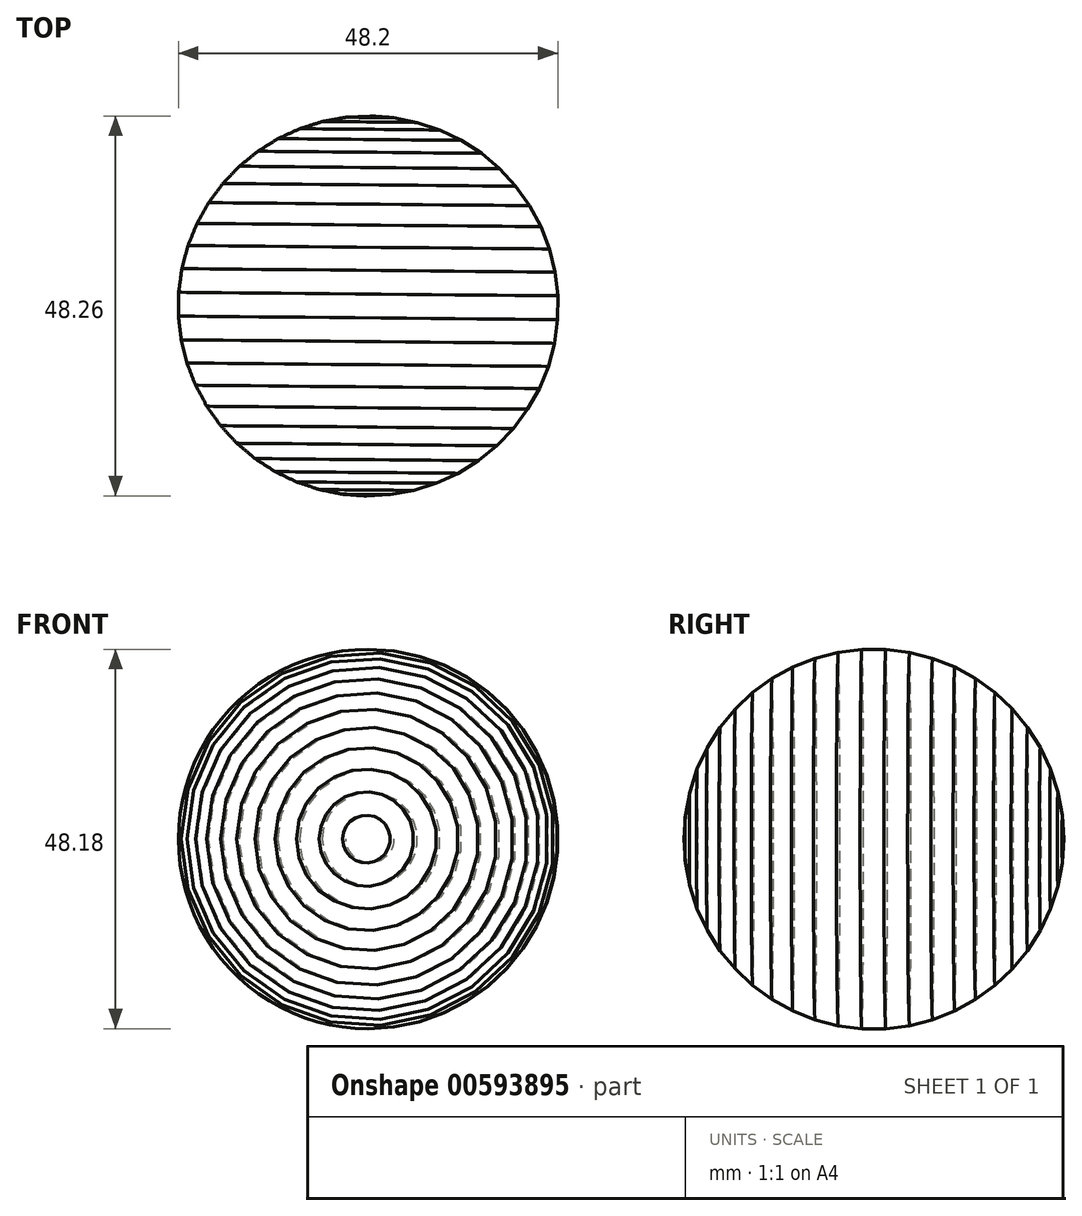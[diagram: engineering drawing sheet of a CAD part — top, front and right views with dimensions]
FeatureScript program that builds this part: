
annotation { "Feature Type Name" : "Feature", "Feature Type Description" : "" }
export const myFeature = defineFeature(function(context is Context, id is Id, definition is map)
    precondition{}
    {
        {
            var Q0;
            Q0=qCreatedBy(makeId("Top.planeOp"),FACE);
            var sketch = newSketch(context, id + "F0", { "sketchPlane" : qUnion([Q0])});
            skCircle(sketch, "E0.cCircle", {"center": v(0, 0) * mm, "radius": 24.09 * mm, "construction": true});
            skLineSegment(sketch, "E0.0", {"start": v(-21.74, 10.48) * mm, "end": v(-20.26, 13.12) * mm});
            skLineSegment(sketch, "E0.1", {"start": v(-20.26, 13.12) * mm, "end": v(-18.45, 15.56) * mm});
            skLineSegment(sketch, "E0.2", {"start": v(-18.45, 15.56) * mm, "end": v(-16.36, 17.75) * mm});
            skLineSegment(sketch, "E0.3", {"start": v(-16.36, 17.75) * mm, "end": v(-14, 19.66) * mm});
            skLineSegment(sketch, "E0.4", {"start": v(-14, 19.66) * mm, "end": v(-11.43, 21.26) * mm});
            skLineSegment(sketch, "E0.5", {"start": v(-11.43, 21.26) * mm, "end": v(-8.67, 22.52) * mm});
            skLineSegment(sketch, "E0.6", {"start": v(-8.67, 22.52) * mm, "end": v(-5.78, 23.43) * mm});
            skLineSegment(sketch, "E0.7", {"start": v(-5.78, 23.43) * mm, "end": v(-2.8, 23.97) * mm});
            skLineSegment(sketch, "E0.8", {"start": v(-2.8, 23.97) * mm, "end": v(0.23, 24.13) * mm});
            skLineSegment(sketch, "E0.9", {"start": v(0.23, 24.13) * mm, "end": v(3.25, 23.92) * mm});
            skLineSegment(sketch, "E0.10", {"start": v(3.25, 23.92) * mm, "end": v(6.22, 23.32) * mm});
            skLineSegment(sketch, "E0.11", {"start": v(6.22, 23.32) * mm, "end": v(9.1, 22.36) * mm});
            skLineSegment(sketch, "E0.12", {"start": v(9.1, 22.36) * mm, "end": v(11.83, 21.04) * mm});
            skLineSegment(sketch, "E0.13", {"start": v(11.83, 21.04) * mm, "end": v(14.37, 19.4) * mm});
            skLineSegment(sketch, "E0.14", {"start": v(14.37, 19.4) * mm, "end": v(16.69, 17.44) * mm});
            skLineSegment(sketch, "E0.15", {"start": v(16.69, 17.44) * mm, "end": v(18.74, 15.2) * mm});
            skLineSegment(sketch, "E0.16", {"start": v(18.74, 15.2) * mm, "end": v(20.5, 12.74) * mm});
            skLineSegment(sketch, "E0.17", {"start": v(20.5, 12.74) * mm, "end": v(21.93, 10.07) * mm});
            skLineSegment(sketch, "E0.18", {"start": v(21.93, 10.07) * mm, "end": v(23.02, 7.24) * mm});
            skLineSegment(sketch, "E0.19", {"start": v(23.02, 7.24) * mm, "end": v(23.75, 4.3) * mm});
            skLineSegment(sketch, "E0.20", {"start": v(23.75, 4.3) * mm, "end": v(24.1, 1.29) * mm});
            skLineSegment(sketch, "E0.21", {"start": v(24.1, 1.29) * mm, "end": v(24.07, -1.74) * mm});
            skLineSegment(sketch, "E0.22", {"start": v(24.07, -1.74) * mm, "end": v(23.66, -4.74) * mm});
            skLineSegment(sketch, "E0.23", {"start": v(23.66, -4.74) * mm, "end": v(22.88, -7.67) * mm});
            skLineSegment(sketch, "E0.24", {"start": v(22.88, -7.67) * mm, "end": v(21.74, -10.48) * mm});
            skLineSegment(sketch, "E0.25", {"start": v(21.74, -10.48) * mm, "end": v(20.26, -13.12) * mm});
            skLineSegment(sketch, "E0.26", {"start": v(20.26, -13.12) * mm, "end": v(18.45, -15.56) * mm});
            skLineSegment(sketch, "E0.27", {"start": v(18.45, -15.56) * mm, "end": v(16.36, -17.75) * mm});
            skLineSegment(sketch, "E0.28", {"start": v(16.36, -17.75) * mm, "end": v(14, -19.66) * mm});
            skLineSegment(sketch, "E0.29", {"start": v(14, -19.66) * mm, "end": v(11.43, -21.26) * mm});
            skLineSegment(sketch, "E0.30", {"start": v(11.43, -21.26) * mm, "end": v(8.67, -22.52) * mm});
            skLineSegment(sketch, "E0.31", {"start": v(8.67, -22.52) * mm, "end": v(5.78, -23.43) * mm});
            skLineSegment(sketch, "E0.32", {"start": v(5.78, -23.43) * mm, "end": v(2.8, -23.97) * mm});
            skLineSegment(sketch, "E0.33", {"start": v(2.8, -23.97) * mm, "end": v(-0.23, -24.13) * mm});
            skLineSegment(sketch, "E0.34", {"start": v(-0.23, -24.13) * mm, "end": v(-3.25, -23.92) * mm});
            skLineSegment(sketch, "E0.35", {"start": v(-3.25, -23.92) * mm, "end": v(-6.22, -23.32) * mm});
            skLineSegment(sketch, "E0.36", {"start": v(-6.22, -23.32) * mm, "end": v(-9.1, -22.36) * mm});
            skLineSegment(sketch, "E0.37", {"start": v(-9.1, -22.36) * mm, "end": v(-11.83, -21.04) * mm});
            skLineSegment(sketch, "E0.38", {"start": v(-11.83, -21.04) * mm, "end": v(-14.37, -19.4) * mm});
            skLineSegment(sketch, "E0.39", {"start": v(-14.37, -19.4) * mm, "end": v(-16.69, -17.44) * mm});
            skLineSegment(sketch, "E0.40", {"start": v(-16.69, -17.44) * mm, "end": v(-18.74, -15.2) * mm});
            skLineSegment(sketch, "E0.41", {"start": v(-18.74, -15.2) * mm, "end": v(-20.5, -12.74) * mm});
            skLineSegment(sketch, "E0.42", {"start": v(-20.5, -12.74) * mm, "end": v(-21.93, -10.07) * mm});
            skLineSegment(sketch, "E0.43", {"start": v(-21.93, -10.07) * mm, "end": v(-23.02, -7.24) * mm});
            skLineSegment(sketch, "E0.44", {"start": v(-23.02, -7.24) * mm, "end": v(-23.75, -4.3) * mm});
            skLineSegment(sketch, "E0.45", {"start": v(-23.75, -4.3) * mm, "end": v(-24.1, -1.29) * mm});
            skLineSegment(sketch, "E0.46", {"start": v(-24.1, -1.29) * mm, "end": v(-24.07, 1.74) * mm});
            skLineSegment(sketch, "E0.47", {"start": v(-24.07, 1.74) * mm, "end": v(-23.66, 4.74) * mm});
            skLineSegment(sketch, "E0.48", {"start": v(-23.66, 4.74) * mm, "end": v(-22.88, 7.67) * mm});
            skLineSegment(sketch, "E0.49", {"start": v(-22.88, 7.67) * mm, "end": v(-21.74, 10.48) * mm});
            skPoint(sketch, "E0.0.midPoint", {"position": v(-21, 11.8) * mm});
            skLineSegment(sketch, "E1", {"start": v(0.23, 24.13) * mm, "end": v(-0.23, -24.13) * mm});
            skSolve(sketch);
        }
        {
            var Q0;
            Q0=makeQuery(id+"F0.imprint","IMPRINT",FACE,{"disambiguationData":[TD([[makeQuery(id+"F0.imprint","IMPRINT",EDGE,{"derivedFrom":sQuery(id+"F0.wireOp",EDGE,"E0.0")}),-1.0]])]});
            var Q1;
            Q1=sQuery(id+"F0.wireOp",EDGE,"E1");
            revolve(context, id + "F1", {"entities" : qUnion([Q0]), "axis" : qUnion([Q1]), "revolveType" : RevolveType.FULL});
        }
    });
